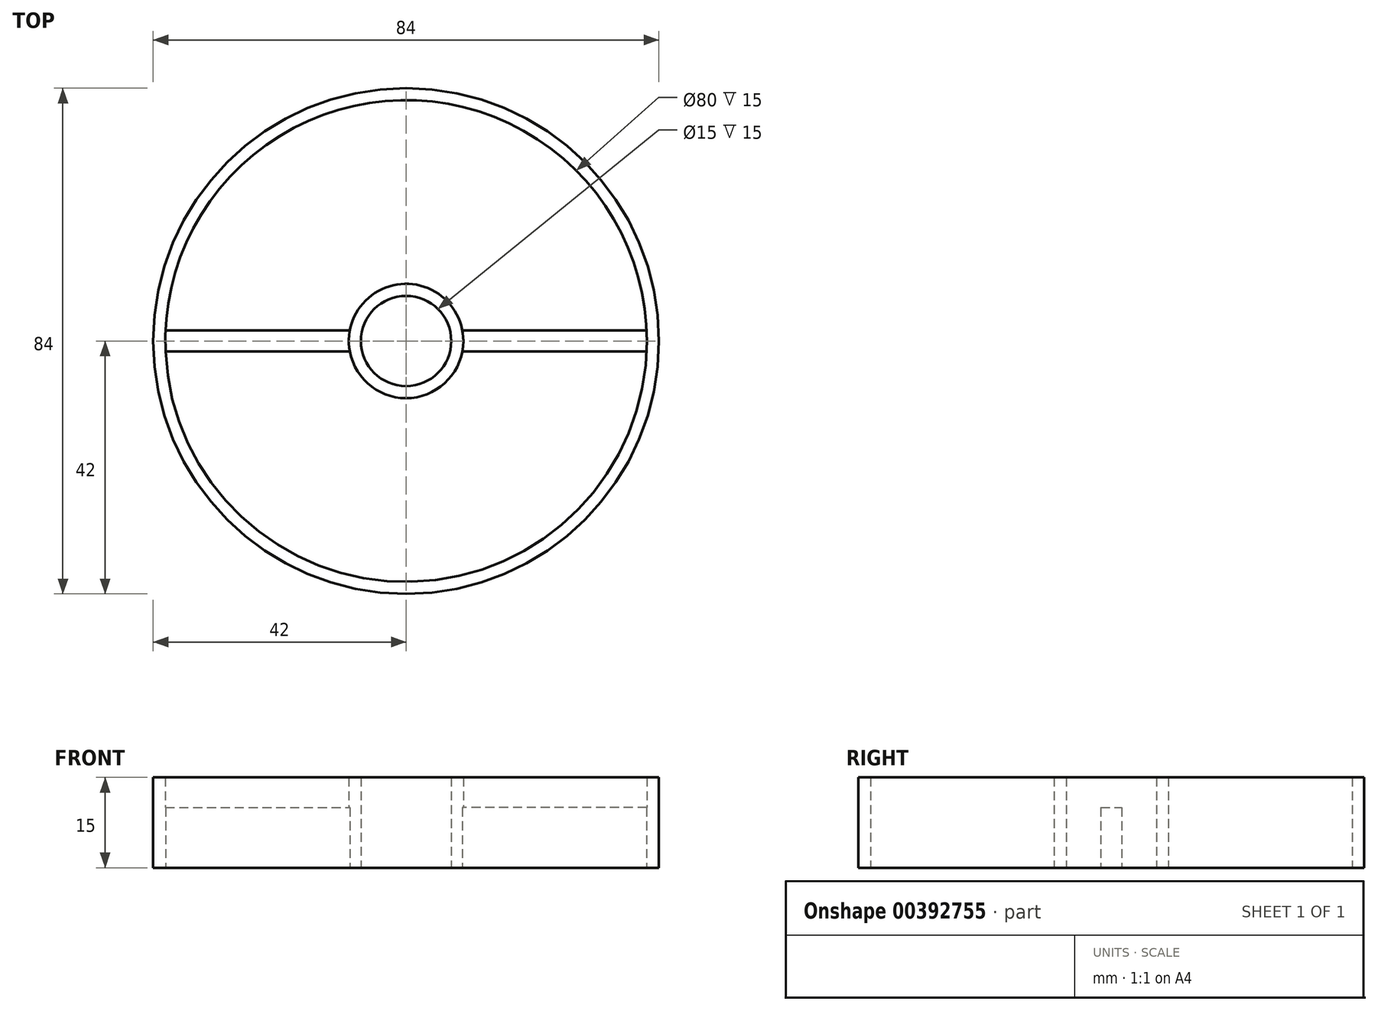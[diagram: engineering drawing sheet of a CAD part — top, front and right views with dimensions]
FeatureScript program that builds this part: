
annotation { "Feature Type Name" : "Feature", "Feature Type Description" : "" }
export const myFeature = defineFeature(function(context is Context, id is Id, definition is map)
    precondition{}
    {
        {
            var Q0;
            Q0=qCreatedBy(makeId("Top.planeOp"),FACE);
            var sketch = newSketch(context, id + "F0", { "sketchPlane" : qUnion([Q0])});
            skCircle(sketch, "E0", {"center": v(0, 0) * mm, "radius": 40 * mm});
            skCircle(sketch, "E1.0", {"center": v(0, 0) * mm, "radius": 42 * mm});
            skCircle(sketch, "E2", {"center": v(0, 0) * mm, "radius": 7.5 * mm});
            skCircle(sketch, "E3.0", {"center": v(0, 0) * mm, "radius": 9.5 * mm});
            skSolve(sketch);
        }
        {
            var Q0;
            Q0=makeQuery(id+"F0.imprint","IMPRINT",FACE,{"disambiguationData":[TD([[makeQuery(id+"F0.imprint","IMPRINT",EDGE,{"derivedFrom":sQuery(id+"F0.wireOp",EDGE,"E0")}),-1.0]])]});
            var Q1;
            Q1=makeQuery(id+"F0.imprint","IMPRINT",FACE,{"disambiguationData":[TD([[makeQuery(id+"F0.imprint","IMPRINT",EDGE,{"derivedFrom":sQuery(id+"F0.wireOp",EDGE,"E2")}),-1.0]])]});
            extrude(context, id + "F1", {"entities" : qUnion([Q0, Q1]), "depth" : 15 * mm});
        }
        {
            var Q0;
            Q0=qCreatedBy(makeId("Top.planeOp"),FACE);
            var sketch = newSketch(context, id + "F2", { "sketchPlane" : qUnion([Q0])});
            skCircle(sketch, "E4.0", {"center": v(0, 0) * mm, "radius": 42 * mm});
            skCircle(sketch, "E5.0", {"center": v(0, 0) * mm, "radius": 47 * mm});
            skCircle(sketch, "E6.0", {"center": v(0, 0) * mm, "radius": 40 * mm});
            skCircle(sketch, "E7.0", {"center": v(0, 0) * mm, "radius": 9.5 * mm});
            skCircle(sketch, "E8.0", {"center": v(0, 0) * mm, "radius": 7.5 * mm});
            skLineSegment(sketch, "E9", {"start": v(-9.34, -1.75) * mm, "end": v(-39.96, -1.75) * mm});
            skLineSegment(sketch, "E10", {"start": v(-39.96, 1.75) * mm, "end": v(-9.34, 1.75) * mm});
            skLineSegment(sketch, "E11", {"start": v(0, 47) * mm, "end": v(0, -47) * mm, "construction": true});
            skLineSegment(sketch, "E12.MirrorCS", {"start": v(39.96, 1.75) * mm, "end": v(9.34, 1.75) * mm});
            skLineSegment(sketch, "E13.MirrorCS", {"start": v(9.34, -1.75) * mm, "end": v(39.96, -1.75) * mm});
            skSolve(sketch);
        }
        {
            var Q0;
            {var subQ0=sQuery(id+"F2.wireOp",EDGE,"E12.MirrorCS");Q0=makeQuery(id+"F2.imprint","IMPRINT",FACE,{"disambiguationData":[TD([[makeQuery(id+"F2.imprint","IMPRINT",EDGE,{"derivedFrom":subQ0}),1.0]])]});}
            var Q1;
            {var subQ0=sQuery(id+"F2.wireOp",EDGE,"E9");Q1=makeQuery(id+"F2.imprint","IMPRINT",FACE,{"disambiguationData":[TD([[makeQuery(id+"F2.imprint","IMPRINT",EDGE,{"derivedFrom":subQ0}),-1.0]])]});}
            extrude(context, id + "F3", {"entities" : qUnion([Q0, Q1]), "operationType" : NewBodyOperationType.ADD, "depth" : 10 * mm});
        }
    });
